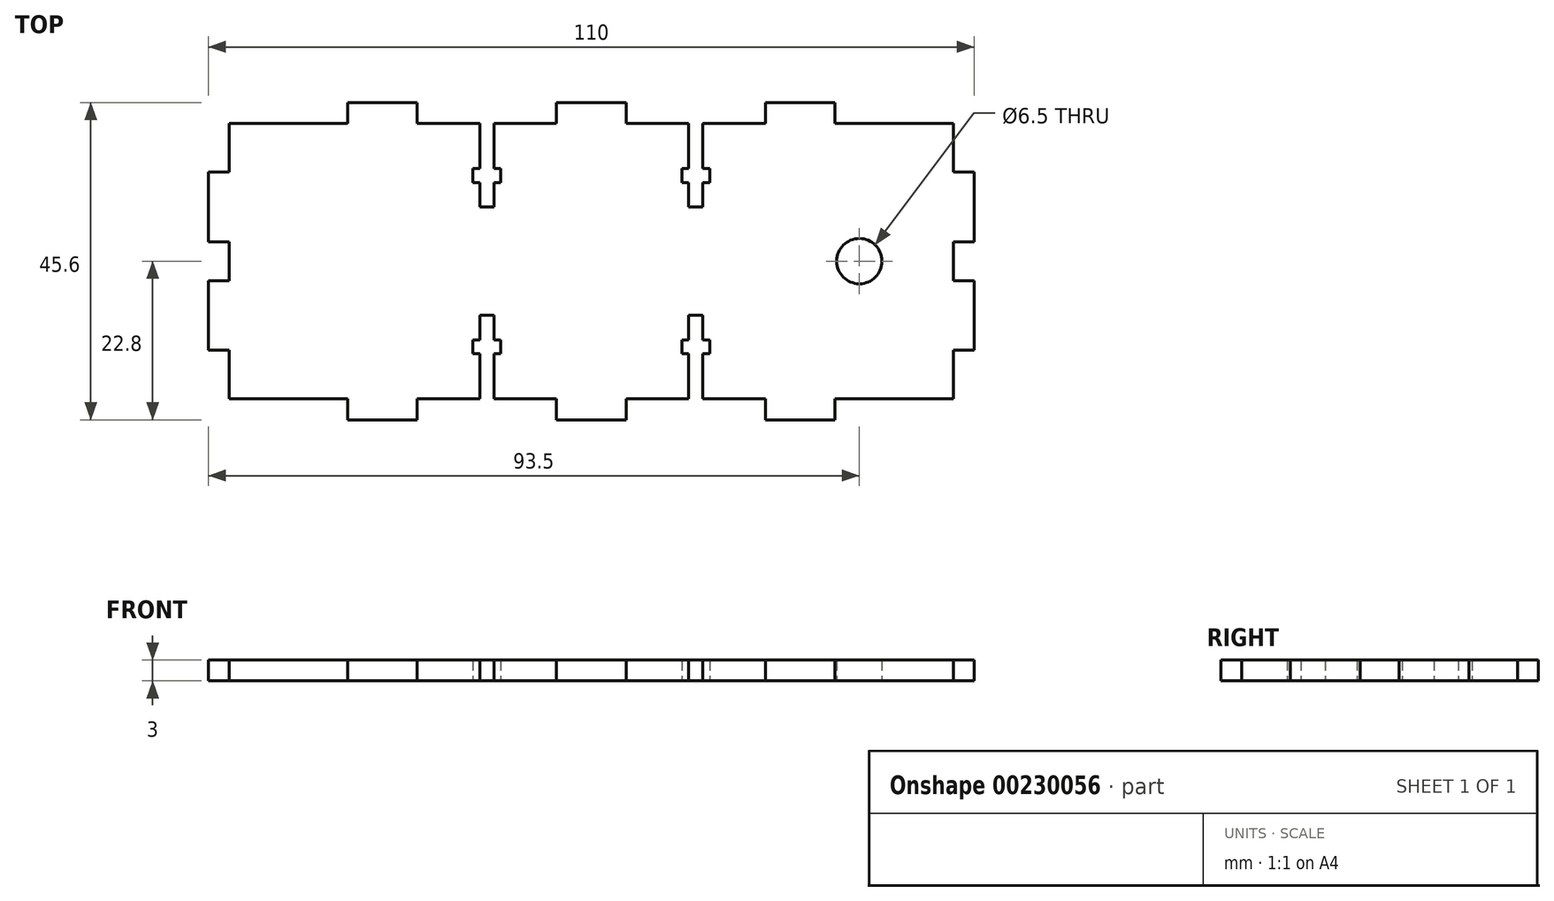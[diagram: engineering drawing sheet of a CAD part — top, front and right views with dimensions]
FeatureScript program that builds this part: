
annotation { "Feature Type Name" : "Feature", "Feature Type Description" : "" }
export const myFeature = defineFeature(function(context is Context, id is Id, definition is map)
    precondition{}
    {
        {
            var Q0;
            Q0=qCreatedBy(makeId("Top.planeOp"),FACE);
            var sketch = newSketch(context, id + "F0", { "sketchPlane" : qUnion([Q0])});
            skLineSegment(sketch, "E0", {"start": v(0, 0) * mm, "end": v(17, 0) * mm});
            skLineSegment(sketch, "E1", {"start": v(17, 0) * mm, "end": v(17, -3) * mm});
            skLineSegment(sketch, "E2", {"start": v(17, -3) * mm, "end": v(27, -3) * mm});
            skLineSegment(sketch, "E3", {"start": v(27, -3) * mm, "end": v(27, 0) * mm});
            skLineSegment(sketch, "E4", {"start": v(47, 0) * mm, "end": v(47, -3) * mm});
            skLineSegment(sketch, "E5", {"start": v(47, -3) * mm, "end": v(57, -3) * mm});
            skLineSegment(sketch, "E6", {"start": v(57, -3) * mm, "end": v(57, 0) * mm});
            skLineSegment(sketch, "E7", {"start": v(77, 0) * mm, "end": v(77, -3) * mm});
            skLineSegment(sketch, "E8", {"start": v(77, -3) * mm, "end": v(87, -3) * mm});
            skLineSegment(sketch, "E9", {"start": v(87, -3) * mm, "end": v(87, 0) * mm});
            skLineSegment(sketch, "E10", {"start": v(87, 0) * mm, "end": v(104, 0) * mm});
            skLineSegment(sketch, "E11", {"start": v(104, 0) * mm, "end": v(104, 7) * mm});
            skLineSegment(sketch, "E12", {"start": v(104, 7) * mm, "end": v(107, 7) * mm});
            skLineSegment(sketch, "E13", {"start": v(107, 7) * mm, "end": v(107, 17) * mm});
            skLineSegment(sketch, "E14", {"start": v(107, 17) * mm, "end": v(104, 17) * mm});
            skLineSegment(sketch, "E15", {"start": v(104, 17) * mm, "end": v(104, 22.6) * mm});
            skLineSegment(sketch, "E16", {"start": v(104, 22.6) * mm, "end": v(107, 22.6) * mm});
            skLineSegment(sketch, "E17", {"start": v(107, 22.6) * mm, "end": v(107, 32.6) * mm});
            skLineSegment(sketch, "E18", {"start": v(107, 32.6) * mm, "end": v(104, 32.6) * mm});
            skLineSegment(sketch, "E19", {"start": v(104, 32.6) * mm, "end": v(104, 39.6) * mm});
            skLineSegment(sketch, "E20", {"start": v(104, 39.6) * mm, "end": v(87, 39.6) * mm});
            skLineSegment(sketch, "E21", {"start": v(87, 39.6) * mm, "end": v(87, 42.6) * mm});
            skLineSegment(sketch, "E22", {"start": v(87, 42.6) * mm, "end": v(77, 42.6) * mm});
            skLineSegment(sketch, "E23", {"start": v(77, 42.6) * mm, "end": v(77, 39.6) * mm});
            skLineSegment(sketch, "E24", {"start": v(57, 39.6) * mm, "end": v(57, 42.6) * mm});
            skLineSegment(sketch, "E25", {"start": v(57, 42.6) * mm, "end": v(47, 42.6) * mm});
            skLineSegment(sketch, "E26", {"start": v(47, 42.6) * mm, "end": v(47, 39.6) * mm});
            skLineSegment(sketch, "E27", {"start": v(27, 39.6) * mm, "end": v(27, 42.6) * mm});
            skLineSegment(sketch, "E28", {"start": v(27, 42.6) * mm, "end": v(17, 42.6) * mm});
            skLineSegment(sketch, "E29", {"start": v(17, 42.6) * mm, "end": v(17, 39.6) * mm});
            skLineSegment(sketch, "E30", {"start": v(17, 39.6) * mm, "end": v(0, 39.6) * mm});
            skLineSegment(sketch, "E31", {"start": v(0, 39.6) * mm, "end": v(0, 32.6) * mm});
            skLineSegment(sketch, "E32", {"start": v(0, 32.6) * mm, "end": v(-3, 32.6) * mm});
            skLineSegment(sketch, "E33", {"start": v(-3, 32.6) * mm, "end": v(-3, 22.6) * mm});
            skLineSegment(sketch, "E34", {"start": v(-3, 22.6) * mm, "end": v(0, 22.6) * mm});
            skLineSegment(sketch, "E35", {"start": v(0, 22.6) * mm, "end": v(0, 17) * mm});
            skLineSegment(sketch, "E36", {"start": v(0, 17) * mm, "end": v(-3, 17) * mm});
            skLineSegment(sketch, "E37", {"start": v(-3, 17) * mm, "end": v(-3, 7) * mm});
            skLineSegment(sketch, "E38", {"start": v(-3, 7) * mm, "end": v(0, 7) * mm});
            skLineSegment(sketch, "E39", {"start": v(0, 7) * mm, "end": v(0, 0) * mm});
            skLineSegment(sketch, "E40.top", {"start": v(36, 12) * mm, "end": v(38, 12) * mm});
            skLineSegment(sketch, "E41.left", {"start": v(35, 8.5) * mm, "end": v(35, 6.5) * mm});
            skLineSegment(sketch, "E41.right", {"start": v(39, 8.5) * mm, "end": v(39, 6.5) * mm});
            skLineSegment(sketch, "E42", {"start": v(35, 8.5) * mm, "end": v(36, 8.5) * mm});
            skLineSegment(sketch, "E43", {"start": v(35, 6.5) * mm, "end": v(36, 6.5) * mm});
            skLineSegment(sketch, "E44", {"start": v(39, 6.5) * mm, "end": v(38, 6.5) * mm});
            skLineSegment(sketch, "E45", {"start": v(39, 8.5) * mm, "end": v(38, 8.5) * mm});
            skLineSegment(sketch, "E46", {"start": v(36, 6.5) * mm, "end": v(36, 0) * mm});
            skLineSegment(sketch, "E47", {"start": v(36, 12) * mm, "end": v(36, 8.5) * mm});
            skLineSegment(sketch, "E48", {"start": v(38, 12) * mm, "end": v(38, 8.5) * mm});
            skLineSegment(sketch, "E49", {"start": v(38, 6.5) * mm, "end": v(38, 0) * mm});
            skLineSegment(sketch, "E50", {"start": v(27, 0) * mm, "end": v(36, 0) * mm});
            skLineSegment(sketch, "E51", {"start": v(38, 0) * mm, "end": v(47, 0) * mm});
            skLineSegment(sketch, "E52.MirrorCS", {"start": v(36, 27.6) * mm, "end": v(38, 27.6) * mm});
            skLineSegment(sketch, "E53.MirrorCS", {"start": v(35, 31.1) * mm, "end": v(35, 33.1) * mm});
            skLineSegment(sketch, "E54.MirrorCS", {"start": v(35, 31.1) * mm, "end": v(36, 31.1) * mm});
            skLineSegment(sketch, "E55.MirrorCS", {"start": v(39, 31.1) * mm, "end": v(38, 31.1) * mm});
            skLineSegment(sketch, "E56.MirrorCS", {"start": v(35, 33.1) * mm, "end": v(36, 33.1) * mm});
            skLineSegment(sketch, "E57.MirrorCS", {"start": v(39, 33.1) * mm, "end": v(38, 33.1) * mm});
            skLineSegment(sketch, "E58.MirrorCS", {"start": v(39, 31.1) * mm, "end": v(39, 33.1) * mm});
            skLineSegment(sketch, "E59.MirrorCS", {"start": v(36, 27.6) * mm, "end": v(36, 31.1) * mm});
            skLineSegment(sketch, "E60.MirrorCS", {"start": v(36, 33.1) * mm, "end": v(36, 39.6) * mm});
            skLineSegment(sketch, "E61.MirrorCS", {"start": v(38, 27.6) * mm, "end": v(38, 31.1) * mm});
            skLineSegment(sketch, "E62.MirrorCS", {"start": v(38, 33.1) * mm, "end": v(38, 39.6) * mm});
            skLineSegment(sketch, "E63", {"start": v(27, 39.6) * mm, "end": v(36, 39.6) * mm});
            skLineSegment(sketch, "E64", {"start": v(38, 39.6) * mm, "end": v(47, 39.6) * mm});
            skLineSegment(sketch, "E65.MirrorCS", {"start": v(68, 12) * mm, "end": v(66, 12) * mm});
            skLineSegment(sketch, "E66.MirrorCS", {"start": v(68, 27.6) * mm, "end": v(66, 27.6) * mm});
            skLineSegment(sketch, "E67.MirrorCS", {"start": v(69, 8.5) * mm, "end": v(68, 8.5) * mm});
            skLineSegment(sketch, "E68.MirrorCS", {"start": v(69, 31.1) * mm, "end": v(69, 33.1) * mm});
            skLineSegment(sketch, "E69.MirrorCS", {"start": v(65, 6.5) * mm, "end": v(66, 6.5) * mm});
            skLineSegment(sketch, "E70.MirrorCS", {"start": v(69, 6.5) * mm, "end": v(68, 6.5) * mm});
            skLineSegment(sketch, "E71.MirrorCS", {"start": v(65, 31.1) * mm, "end": v(65, 33.1) * mm});
            skLineSegment(sketch, "E72.MirrorCS", {"start": v(69, 33.1) * mm, "end": v(68, 33.1) * mm});
            skLineSegment(sketch, "E73.MirrorCS", {"start": v(69, 8.5) * mm, "end": v(69, 6.5) * mm});
            skLineSegment(sketch, "E74.MirrorCS", {"start": v(69, 31.1) * mm, "end": v(68, 31.1) * mm});
            skLineSegment(sketch, "E75.MirrorCS", {"start": v(65, 8.5) * mm, "end": v(65, 6.5) * mm});
            skLineSegment(sketch, "E76.MirrorCS", {"start": v(65, 33.1) * mm, "end": v(66, 33.1) * mm});
            skLineSegment(sketch, "E77.MirrorCS", {"start": v(65, 8.5) * mm, "end": v(66, 8.5) * mm});
            skLineSegment(sketch, "E78.MirrorCS", {"start": v(65, 31.1) * mm, "end": v(66, 31.1) * mm});
            skLineSegment(sketch, "E79.MirrorCS", {"start": v(66, 12) * mm, "end": v(66, 8.5) * mm});
            skLineSegment(sketch, "E80.MirrorCS", {"start": v(66, 27.6) * mm, "end": v(66, 31.1) * mm});
            skLineSegment(sketch, "E81.MirrorCS", {"start": v(66, 33.1) * mm, "end": v(66, 39.6) * mm});
            skLineSegment(sketch, "E82.MirrorCS", {"start": v(68, 12) * mm, "end": v(68, 8.5) * mm});
            skLineSegment(sketch, "E83.MirrorCS", {"start": v(66, 6.5) * mm, "end": v(66, 0) * mm});
            skLineSegment(sketch, "E84.MirrorCS", {"start": v(68, 6.5) * mm, "end": v(68, 0) * mm});
            skLineSegment(sketch, "E85.MirrorCS", {"start": v(68, 33.1) * mm, "end": v(68, 39.6) * mm});
            skLineSegment(sketch, "E86.MirrorCS", {"start": v(68, 27.6) * mm, "end": v(68, 31.1) * mm});
            skLineSegment(sketch, "E87", {"start": v(57, 0) * mm, "end": v(66, 0) * mm});
            skLineSegment(sketch, "E88", {"start": v(68, 0) * mm, "end": v(77, 0) * mm});
            skLineSegment(sketch, "E89", {"start": v(57, 39.6) * mm, "end": v(66, 39.6) * mm});
            skLineSegment(sketch, "E90", {"start": v(68, 39.6) * mm, "end": v(77, 39.6) * mm});
            skCircle(sketch, "E91", {"center": v(90.5, 19.8) * mm, "radius": 3.25 * mm});
            skSolve(sketch);
        }
        {
            var Q0;
            Q0 = qSketchRegion(id + "F0", true);
            extrude(context, id + "F1", {"entities" : qUnion([Q0]), "depth" : 3 * mm});
        }
    });
